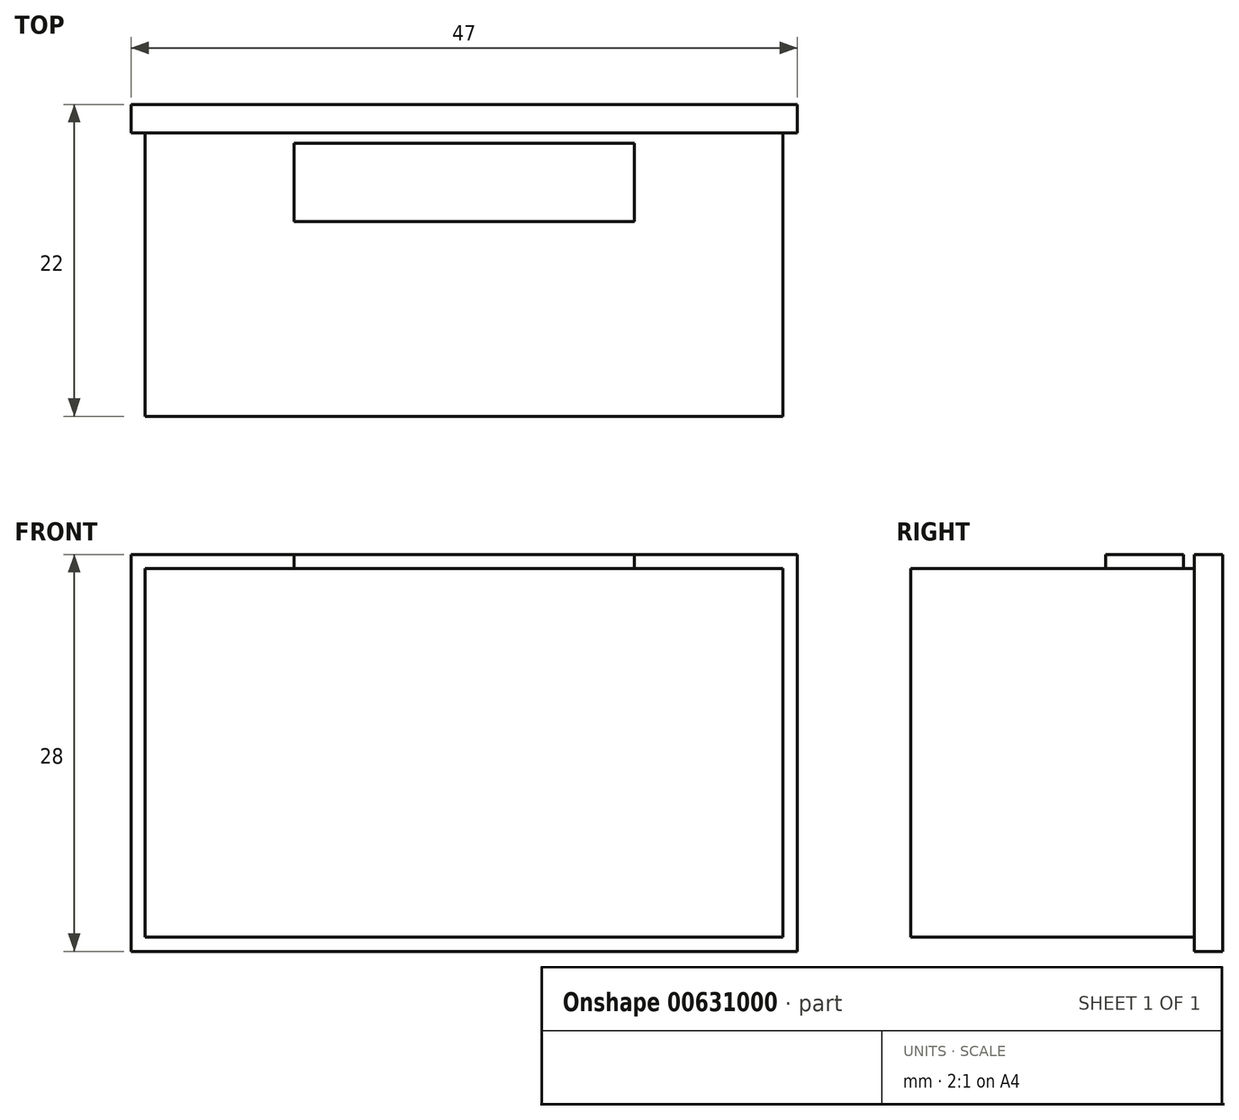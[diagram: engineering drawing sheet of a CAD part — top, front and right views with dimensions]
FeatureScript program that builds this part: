
annotation { "Feature Type Name" : "Feature", "Feature Type Description" : "" }
export const myFeature = defineFeature(function(context is Context, id is Id, definition is map)
    precondition{}
    {
        {
            var Q0;
            Q0=qCreatedBy(makeId("Front.planeOp"),FACE);
            var sketch = newSketch(context, id + "F0", { "sketchPlane" : qUnion([Q0])});
            skLineSegment(sketch, "E0.bottom", {"start": v(23.5, -14) * mm, "end": v(-23.5, -14) * mm});
            skLineSegment(sketch, "E0.top", {"start": v(23.5, 14) * mm, "end": v(-23.5, 14) * mm});
            skLineSegment(sketch, "E0.left", {"start": v(23.5, -14) * mm, "end": v(23.5, 14) * mm});
            skLineSegment(sketch, "E0.right", {"start": v(-23.5, -14) * mm, "end": v(-23.5, 14) * mm});
            skPoint(sketch, "E0.middle", {"position": v(0, 0) * mm});
            skLineSegment(sketch, "E1.bottom", {"start": v(22.5, -13) * mm, "end": v(-22.5, -13) * mm});
            skLineSegment(sketch, "E1.top", {"start": v(22.5, 13) * mm, "end": v(-22.5, 13) * mm});
            skLineSegment(sketch, "E1.left", {"start": v(22.5, -13) * mm, "end": v(22.5, 13) * mm});
            skLineSegment(sketch, "E1.right", {"start": v(-22.5, -13) * mm, "end": v(-22.5, 13) * mm});
            skSolve(sketch);
        }
        {
            var Q0;
            Q0=makeQuery(id+"F0.imprint","IMPRINT",FACE,{"disambiguationData":[TD([[makeQuery(id+"F0.imprint","IMPRINT",EDGE,{"derivedFrom":sQuery(id+"F0.wireOp",EDGE,"E1.bottom")}),-1.0]])]});
            extrude(context, id + "F1", {"entities" : qUnion([Q0]), "depth" : 22 * mm, "offsetDistance" : 25 * mm});
        }
        {
            var Q0;
            Q0=makeQuery(id+"F0.imprint","IMPRINT",FACE,{"disambiguationData":[TD([[makeQuery(id+"F0.imprint","IMPRINT",EDGE,{"derivedFrom":sQuery(id+"F0.wireOp",EDGE,"E0.bottom")}),-1.0]])]});
            extrude(context, id + "F2", {"entities" : qUnion([Q0]), "operationType" : NewBodyOperationType.ADD, "depth" : 2 * mm, "offsetDistance" : 25 * mm});
        }
        {
            var Q0;
            Q0=makeQuery(id+"F1.opExtrude","SWEPT_FACE",FACE,{"disambiguationData":[OSD([sQuery(id+"F0.wireOp",EDGE,"E1.top")])]});
            var sketch = newSketch(context, id + "F3", { "sketchPlane" : qUnion([Q0])});
            skLineSegment(sketch, "E2.bottom", {"start": v(12, -8.25) * mm, "end": v(-12, -8.25) * mm});
            skLineSegment(sketch, "E2.top", {"start": v(12, -2.75) * mm, "end": v(-12, -2.75) * mm});
            skLineSegment(sketch, "E2.left", {"start": v(12, -8.25) * mm, "end": v(12, -2.75) * mm});
            skLineSegment(sketch, "E2.right", {"start": v(-12, -8.25) * mm, "end": v(-12, -2.75) * mm});
            skPoint(sketch, "E2.middle", {"position": v(0, -5.5) * mm});
            skSolve(sketch);
        }
        {
            var Q0;
            Q0=makeQuery(id+"F3.imprint","IMPRINT",FACE,{"disambiguationData":[TD([[makeQuery(id+"F3.imprint","IMPRINT",EDGE,{"derivedFrom":sQuery(id+"F3.wireOp",EDGE,"E2.bottom")}),-1.0]])]});
            extrude(context, id + "F4", {"entities" : qUnion([Q0]), "operationType" : NewBodyOperationType.ADD, "depth" : 1 * mm, "offsetDistance" : 25 * mm});
        }
    });
